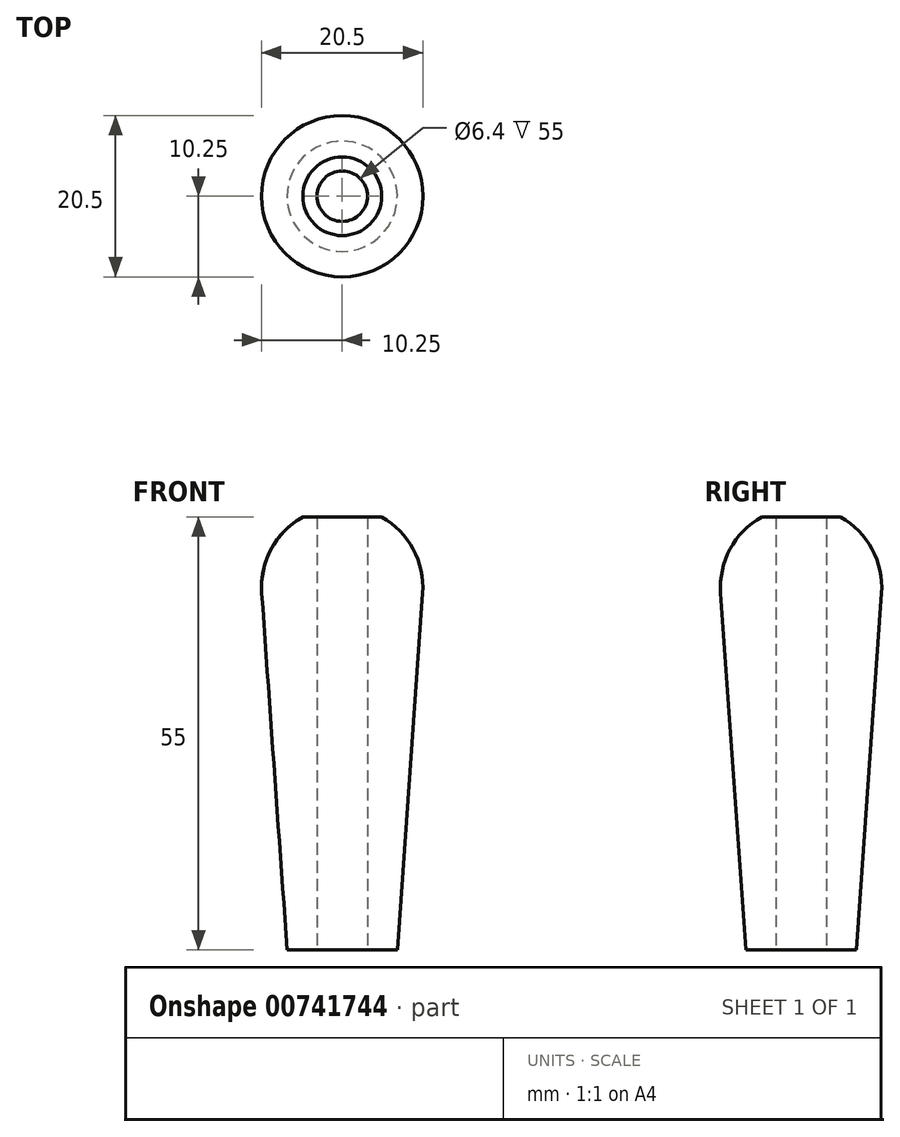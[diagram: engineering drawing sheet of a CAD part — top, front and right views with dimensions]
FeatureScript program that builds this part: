
annotation { "Feature Type Name" : "Feature", "Feature Type Description" : "" }
export const myFeature = defineFeature(function(context is Context, id is Id, definition is map)
    precondition{}
    {
        {
            var Q0;
            Q0=qCreatedBy(makeId("Front.planeOp"),FACE);
            var sketch = newSketch(context, id + "F0", { "sketchPlane" : qUnion([Q0])});
            skLineSegment(sketch, "E0", {"start": v(0, -6) * mm, "end": v(0, 57.85) * mm, "construction": true});
            skLineSegment(sketch, "E1", {"start": v(7, 0) * mm, "end": v(10.22, 45.32) * mm});
            skArc(sketch, "E2", {"start": v(10.22, 45.32) * mm, "mid": v(9.02, 50.92) * mm, "end": v(5, 55) * mm});
            skLineSegment(sketch, "E3", {"start": v(7, 0) * mm, "end": v(3.2, 0) * mm});
            skLineSegment(sketch, "E4", {"start": v(3.2, 0) * mm, "end": v(3.2, 55) * mm});
            skLineSegment(sketch, "E5", {"start": v(3.2, 55) * mm, "end": v(5, 55) * mm});
            skSolve(sketch);
        }
        {
            var Q0;
            Q0=makeQuery(id+"F0.imprint","IMPRINT",FACE,{"disambiguationData":[TD([[makeQuery(id+"F0.imprint","IMPRINT",EDGE,{"derivedFrom":sQuery(id+"F0.wireOp",EDGE,"E1")}),1.0]])]});
            var Q1;
            Q1=sQuery(id+"F0.wireOp",EDGE,"E0");
            revolve(context, id + "F1", {"entities" : qUnion([Q0]), "axis" : qUnion([Q1]), "revolveType" : RevolveType.FULL});
        }
    });
